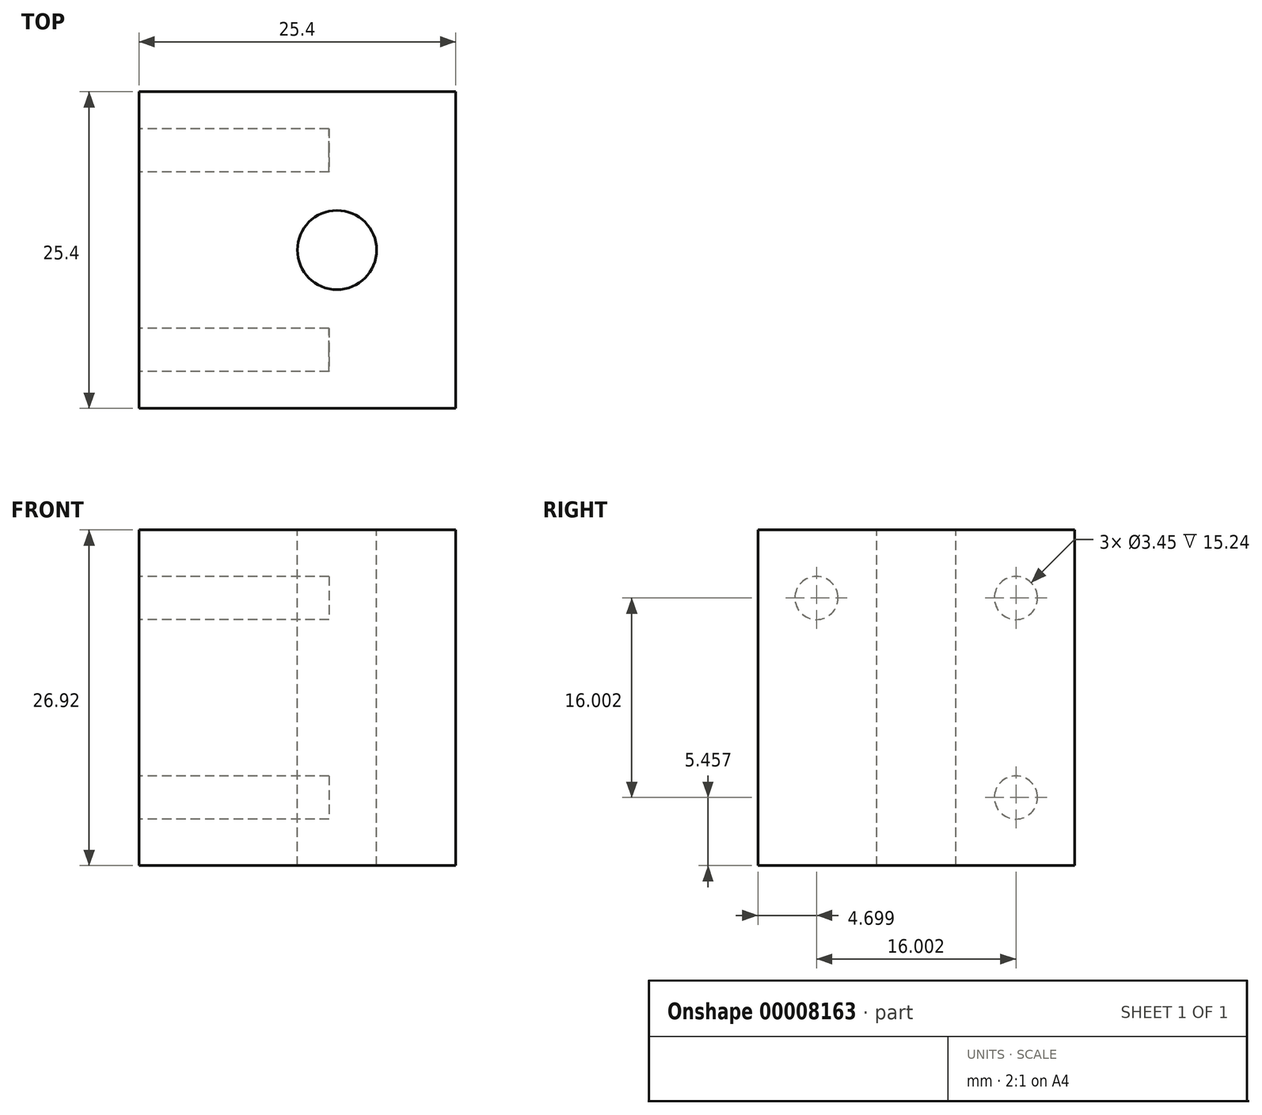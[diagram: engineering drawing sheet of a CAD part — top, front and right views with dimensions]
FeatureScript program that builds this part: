
annotation { "Feature Type Name" : "Feature", "Feature Type Description" : "" }
export const myFeature = defineFeature(function(context is Context, id is Id, definition is map)
    precondition{}
    {
        {
            var Q0;
            Q0=qCreatedBy(makeId("Top.planeOp"),FACE);
            var sketch = newSketch(context, id + "F0", { "sketchPlane" : qUnion([Q0])});
            skLineSegment(sketch, "E0.rect.bottom", {"start": v(12.7, -12.7) * mm, "end": v(-12.7, -12.7) * mm});
            skLineSegment(sketch, "E0.rect.top", {"start": v(12.7, 12.7) * mm, "end": v(-12.7, 12.7) * mm});
            skLineSegment(sketch, "E0.rect.left", {"start": v(12.7, -12.7) * mm, "end": v(12.7, 12.7) * mm});
            skLineSegment(sketch, "E0.rect.right", {"start": v(-12.7, -12.7) * mm, "end": v(-12.7, 12.7) * mm});
            skPoint(sketch, "E0.rect.middle", {"position": v(0, 0) * mm});
            skCircle(sketch, "E1", {"center": v(3.17, 0) * mm, "radius": 3.18 * mm});
            skSolve(sketch);
        }
        {
            var Q0;
            Q0 = qSketchRegion(id + "F0", true);
            extrude(context, id + "F1", {"entities" : qUnion([Q0]), "oppositeDirection" : true, "depth" : 26.92 * mm});
        }
        {
            var Q0;
            Q0=makeQuery(id+"F1.opExtrude","SWEPT_FACE",FACE,{"disambiguationData":[OSD([sQuery(id+"F0.wireOp",EDGE,"E0.rect.right")])]});
            var sketch = newSketch(context, id + "F2", { "sketchPlane" : qUnion([Q0])});
            skCircle(sketch, "E2", {"center": v(-8, -5.46) * mm, "radius": 1.73 * mm});
            skCircle(sketch, "E3", {"center": v(8, -5.46) * mm, "radius": 1.73 * mm});
            skCircle(sketch, "E4", {"center": v(-8, -21.46) * mm, "radius": 1.73 * mm});
            skSolve(sketch);
        }
        {
            var Q0;
            Q0 = qSketchRegion(id + "F2", true);
            extrude(context, id + "F3", {"entities" : qUnion([Q0]), "operationType" : NewBodyOperationType.REMOVE, "oppositeDirection" : true, "depth" : 15.24 * mm});
        }
    });
